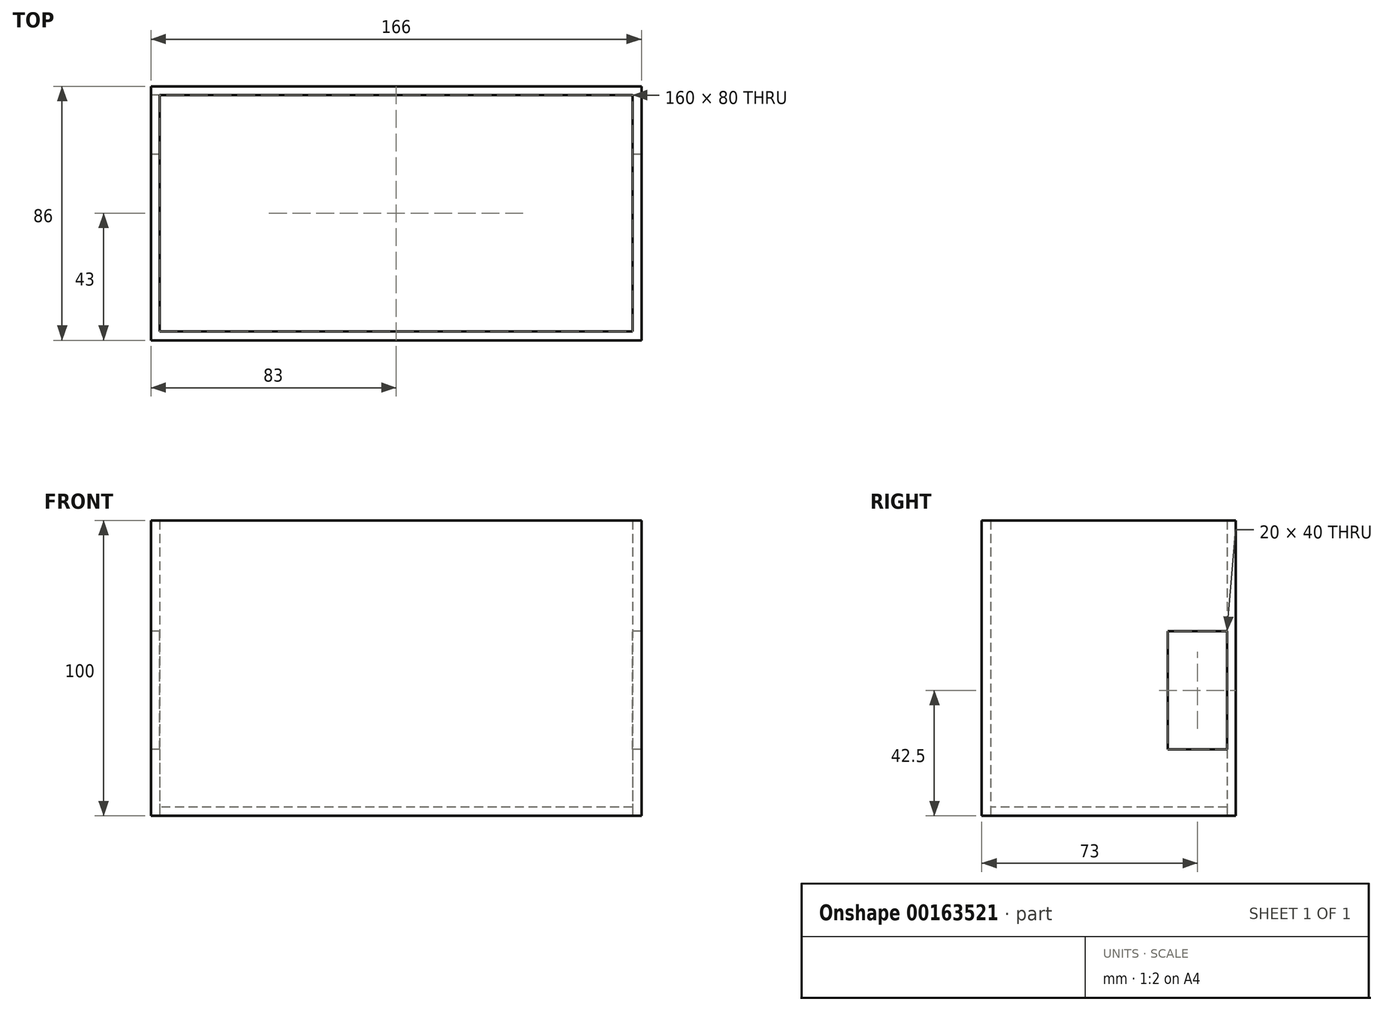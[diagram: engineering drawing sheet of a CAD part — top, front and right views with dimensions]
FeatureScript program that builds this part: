
annotation { "Feature Type Name" : "Feature", "Feature Type Description" : "" }
export const myFeature = defineFeature(function(context is Context, id is Id, definition is map)
    precondition{}
    {
        {
            var Q0;
            Q0=qCreatedBy(makeId("Top.planeOp"),FACE);
            var sketch = newSketch(context, id + "F0", { "sketchPlane" : qUnion([Q0])});
            skLineSegment(sketch, "E0.bottom", {"start": v(80, 40) * mm, "end": v(-80, 40) * mm});
            skLineSegment(sketch, "E0.top", {"start": v(80, -40) * mm, "end": v(-80, -40) * mm});
            skLineSegment(sketch, "E0.left", {"start": v(80, 40) * mm, "end": v(80, -40) * mm});
            skLineSegment(sketch, "E0.right", {"start": v(-80, 40) * mm, "end": v(-80, -40) * mm});
            skPoint(sketch, "E0.middle", {"position": v(0, 0) * mm});
            skLineSegment(sketch, "E1.0", {"start": v(-83, 43) * mm, "end": v(-83, -43) * mm});
            skLineSegment(sketch, "E1.1", {"start": v(83, 43) * mm, "end": v(-83, 43) * mm});
            skLineSegment(sketch, "E1.2", {"start": v(83, 43) * mm, "end": v(83, -43) * mm});
            skLineSegment(sketch, "E1.3", {"start": v(83, -43) * mm, "end": v(-83, -43) * mm});
            skSolve(sketch);
        }
        {
            var Q0;
            Q0=makeQuery(id+"F0.imprint","IMPRINT",FACE,{"disambiguationData":[TD([[makeQuery(id+"F0.imprint","IMPRINT",EDGE,{"derivedFrom":sQuery(id+"F0.wireOp",EDGE,"E0.bottom")}),1.0]])]});
            extrude(context, id + "F1", {"entities" : qUnion([Q0]), "depth" : 3 * mm});
        }
        {
            var Q0;
            Q0=makeQuery(id+"F0.imprint","IMPRINT",FACE,{"disambiguationData":[TD([[makeQuery(id+"F0.imprint","IMPRINT",EDGE,{"derivedFrom":sQuery(id+"F0.wireOp",EDGE,"E0.bottom")}),-1.0]])]});
            extrude(context, id + "F2", {"entities" : qUnion([Q0]), "depth" : 100 * mm});
        }
        {
            var Q0;
            Q0=makeQuery(id+"F2.opExtrude","SWEPT_FACE",FACE,{"disambiguationData":[OSD([sQuery(id+"F0.wireOp",EDGE,"E1.0")])]});
            var sketch = newSketch(context, id + "F3", { "sketchPlane" : qUnion([Q0])});
            skLineSegment(sketch, "E2.bottom", {"start": v(-40, 62.5) * mm, "end": v(-20, 62.5) * mm});
            skLineSegment(sketch, "E2.top", {"start": v(-40, 22.5) * mm, "end": v(-20, 22.5) * mm});
            skLineSegment(sketch, "E2.left", {"start": v(-40, 62.5) * mm, "end": v(-40, 22.5) * mm});
            skLineSegment(sketch, "E2.right", {"start": v(-20, 62.5) * mm, "end": v(-20, 22.5) * mm});
            skSolve(sketch);
        }
        {
            var Q0;
            Q0=makeQuery(id+"F3.imprint","IMPRINT",FACE,{"disambiguationData":[TD([[makeQuery(id+"F3.imprint","IMPRINT",EDGE,{"derivedFrom":sQuery(id+"F3.wireOp",EDGE,"E2.bottom")}),-1.0]])]});
            extrude(context, id + "F4", {"entities" : qUnion([Q0]), "operationType" : NewBodyOperationType.REMOVE, "endBound" : BoundingType.THROUGH_ALL, "oppositeDirection" : true, "depth" : 25 * mm});
        }
        {
            var Q0;
            Q0=makeQuery(id+"F1.opExtrude","CAP_FACE",FACE,{"disambiguationData":[OSD([sQuery(id+"F0.wireOp",EDGE,"E0.bottom"),sQuery(id+"F0.wireOp",EDGE,"E0.top"),sQuery(id+"F0.wireOp",EDGE,"E0.left"),sQuery(id+"F0.wireOp",EDGE,"E0.right")])],"isStart":false});
            var sketch = newSketch(context, id + "F5", { "sketchPlane" : qUnion([Q0])});
            skLineSegment(sketch, "E3.0", {"start": v(-59.1, 40) * mm, "end": v(-59.1, -40) * mm, "construction": true});
            skLineSegment(sketch, "E4.0", {"start": v(59.1, 40) * mm, "end": v(59.1, -40) * mm, "construction": true});
            skPoint(sketch, "E5", {"position": v(59.1, 30) * mm});
            skPoint(sketch, "E6", {"position": v(-59.1, 30) * mm});
            skLineSegment(sketch, "E7.0", {"start": v(80, -30) * mm, "end": v(-80, -30) * mm, "construction": true});
            skPoint(sketch, "E8", {"position": v(-59.1, -30) * mm});
            skPoint(sketch, "E9", {"position": v(59.1, -30) * mm});
            skSolve(sketch);
        }
    });
